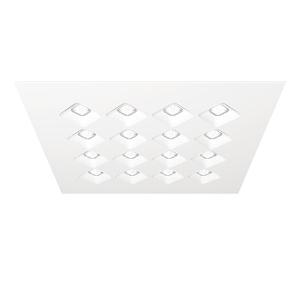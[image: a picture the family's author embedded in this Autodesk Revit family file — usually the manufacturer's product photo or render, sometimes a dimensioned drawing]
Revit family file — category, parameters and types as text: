
# Revit family: 3f_filippi_-_3f_diagon_3f_filippi_-_23386_-_3f_diagon_25w-830_621x621
name_source: partatom
category: Lighting Fixtures
units: mm (PartAtom-declared; Revit-internal decimal feet)

## family parameters
Cut with Voids When Loaded = No
Host = Face
Light Source = No
Part Type = Normal
Room Calculation Point = No
Round Connector Dimension = Use Diameter
Shared = No

## types (1)
- 3F Filippi - 3F Dìagon (1 x LED, 4038 lm, 28 W, 3000 K)
    Apparent Load = 28 VA
    Approval mark = CE
    CIE Flux Codes = 67 96 100 100 100
    Color Rendering = 80
    Color Temperature = 3000 K
    Control Gear = Electronic ballast
    Default Elevation = 1800 mm
    Description = ILLUMINOTECHNICAL
Luminous efficiency 100% (DLOR 100%, ULOR 0%).
Initial luminous flux of the luminaire 4038 lm.
Direct symmetric distribution.
Installation Interdistance Transv.D = 1.39 x hu - Long.D = 1.39 x hu.
Average luminance <1500 cd/m² for radial angles >65°.
Tabular UGR (CIE 117 - 4H-8H; S=0.25H; 70/50/20): RUG 17.2 - 17.2.
Beam angle: 93° - 92°.
Luminous efficacy 144 lm/W.
Lifetime (L95/B10): 30000 h. (tq+25°C)
Lifetime (L90/B10): 50000 h. (tq+25°C)
Lifetime (L80/B10): 80000 h. (tq+25°C)
Lifetime (L75/B10): 100000 h. (tq+25°C)
Sudden decreased luminous flux after 50000 hours: 0% (C0).
Photobiological safety in compliance with IEC/TR 62778: RG0 risk exempt, (IEC 62471).
In compliance with IEC/EN 62722-2-1 - IEC/EN 62717 standards.

SOURCE
Squared LED module 25W/830.
Energy efficiency class (UE 2019/2020 - UE 2019/2015): C.
CIE 13.3 Colour rendering index: CRI >80 (R9 <50%).
IES TM-30 Fidelity Index: Rf = 84 Rg = 95.
CCT nominal colour temperature 3000 K.
Colour initial tolerance (MacAdam): SDCM 3.

MECHANICAL
Housing in hot-galvanised steel, painted in white polyester.
Honeycombed diagonal screen in white anti-glare polycarbonate.
Rhomboidal lenses with differentiated surfaces, etched and prismatic to optimise the orientation of the luminous flux, in transparent methacrylate (PMMA).
Luminaire with limited surface temperature. - D - (EN 60598-2-24)
Dimensions: 621x621 mm, height 30 mm. Weight 3.75 kg.
IP43 protection degree for exposed part, IP20 for recessed part.
Mechanical strength to impacts IK06 (1 joule).
Glow-wire test resistance 650°C.

ELECTRICAL
Halogen Free electronic wiring 230V-50/60Hz, power factor 0.95, THD <25%, constant output current, class I, 1 driver.
Power of the luminaire 28 W.
ENEC - CE.
SAFE FLICKER: PstLM=<1 and SVM=<0.4 (IEC TR 61547-1 and IEC TR 63158), to ensure a more comfortable and safe light.
Luminaire compliant with EN 60598-2-22 for power supply from a centralised emergency system CPSS (Central Power Supply System), not incorporated in the luminaire - high risk areas excluded. The default power and flux are 100% in AC and 100% in DC.
Ambient temperature from 0°C to +25°C.
Temperature class T6 max 85°C.
Quick connection.
Relative humidity UR: <85%.

INSTALLATION
Lay-in recessed fitting.
Height only 30 mm.
Installation on false ceilings with recessed dimensions greater than 596x596 standard size.
Installation after mounting the false ceiling, resting on the exposed structure, minimum void of 140 mm from the lower edge of the structure.
Simultaneous installation with the false ceiling, minimum void of 60 mm from the lower edge of the structure.
All accessories dedicated to this product are available on the Catalog and on our website www.3F-Filippi.com.

APPLICATIONS
Environments: staterooms, with VDTs, offices.
Environments with exacting visual tasks, where diffused soft light for optimum visual comfort is required.

WARNING
Luminaire designed for disposal/recycling at end-of-life.
Replaceable (LED only) light source by a professional. Replaceable control gear by a professional.
    Height = 0 mm  [stored 0 ft]
    Lamp = 1 x LED
    Lamp Light Flux = 4038 lm
    Lamp Power = 28 W
    Lamp count = 1
    Length = 621 mm
    Lifetime = 50000 h
    Luminous efficacy = 144 lm/W
    Manufacturer = 3F Filippi
    ModVariant = No
    Model = 3F Filippi - 23386 - 3F Diagon 25W-830 621x621
    Mounting Place = Ceiling
    Mounting Type = Recessed
    Number of Poles = 1
    OnlyDefault = Yes
    Power Factor = 1
    Product Name = 3F Filippi - 3F Dìagon
    Product group = recessed luminaire
    ProductGroupID = 4
    Protection Class = Protection class I
    Protection Degree = IP 20
    RLX_Detail_Level = 1
    RLX_Emergency_Light_Flux = 0 lm
    RLX_Emergency_Type = 0
    RLX_Emergency_Type_DB = No
    RlxData = <blob elided: 85145 chars, md5=a356106c>
    Socket = socket
    Standby Power = 0 W
    System Light Flux = 4038 lm
    System Power = 28 W
    Type Comments = Product without accessories
    Type Image = 3ffilippi_3f_diagon.jpg
    URL = http://relux.com
    VarID = ---
    Voltage = 0 V
    Weight = 0.00 kg
    Width = 621 mm

note: [stored X ft] marks values corroborated as IEEE doubles in the binary element streams (Revit-internal decimal feet)

## geometry (parser evidence)
native form markers: Blend x4, Sweep x11
no freeform markers — native parametric forms only
